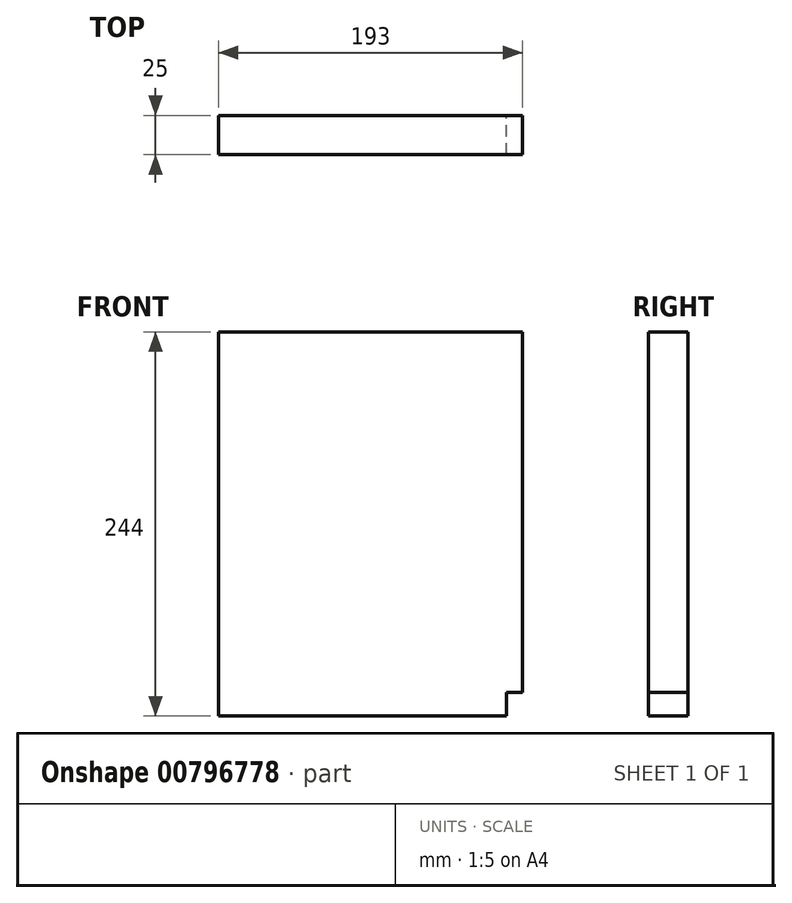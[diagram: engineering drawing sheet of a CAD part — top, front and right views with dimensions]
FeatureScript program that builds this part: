
annotation { "Feature Type Name" : "Feature", "Feature Type Description" : "" }
export const myFeature = defineFeature(function(context is Context, id is Id, definition is map)
    precondition{}
    {
        {
            var Q0;
            Q0=qCreatedBy(makeId("Front.planeOp"),FACE);
            var sketch = newSketch(context, id + "F0", { "sketchPlane" : qUnion([Q0])});
            skLineSegment(sketch, "E0.bottom", {"start": v(-119.27, 190.43) * mm, "end": v(73.73, 190.43) * mm});
            skLineSegment(sketch, "E0.top", {"start": v(-119.27, -53.57) * mm, "end": v(63.73, -53.57) * mm});
            skLineSegment(sketch, "E0.left", {"start": v(-119.27, 190.43) * mm, "end": v(-119.27, -53.57) * mm});
            skLineSegment(sketch, "E0.right", {"start": v(73.73, 190.43) * mm, "end": v(73.73, -38.57) * mm});
            skLineSegment(sketch, "E1.top", {"start": v(73.73, -38.57) * mm, "end": v(63.73, -38.57) * mm});
            skLineSegment(sketch, "E1.right", {"start": v(63.73, -53.57) * mm, "end": v(63.73, -38.57) * mm});
            skSolve(sketch);
        }
        {
            var Q0;
            Q0=makeQuery(id+"F0.imprint","IMPRINT",FACE,{"disambiguationData":[TD([[makeQuery(id+"F0.imprint","IMPRINT",EDGE,{"derivedFrom":sQuery(id+"F0.wireOp",EDGE,"E0.bottom")}),-1.0]])]});
            extrude(context, id + "F1", {"entities" : qUnion([Q0]), "depth" : 25 * mm, "offsetDistance" : 25 * mm});
        }
    });
